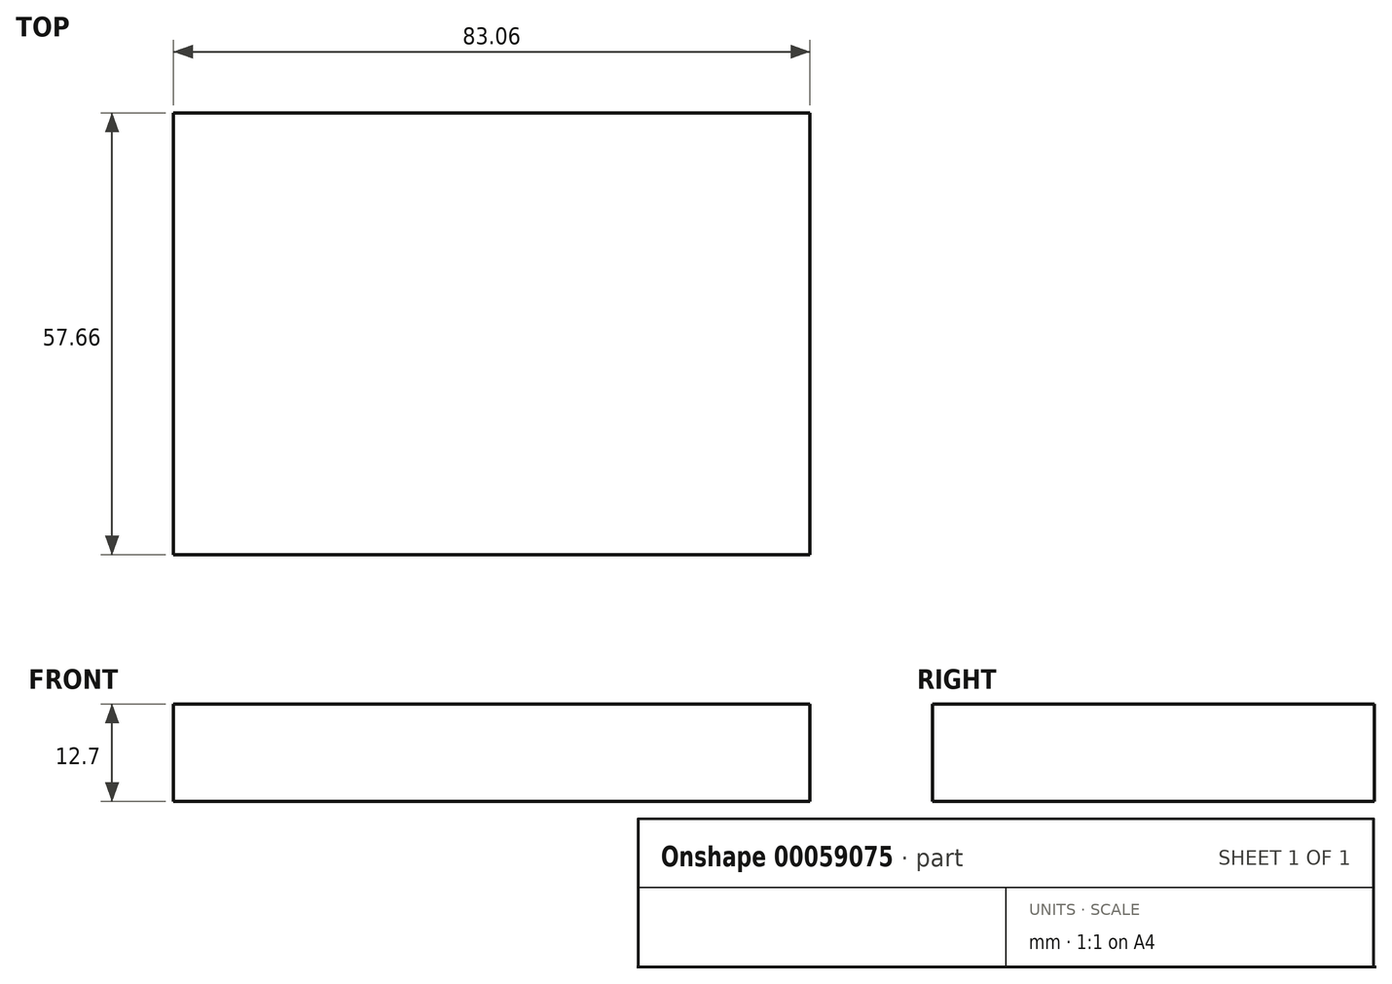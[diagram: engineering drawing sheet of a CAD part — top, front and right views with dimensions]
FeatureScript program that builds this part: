
annotation { "Feature Type Name" : "Feature", "Feature Type Description" : "" }
export const myFeature = defineFeature(function(context is Context, id is Id, definition is map)
    precondition{}
    {
        {
            var Q0;
            Q0=qCreatedBy(makeId("Top.planeOp"),FACE);
            var sketch = newSketch(context, id + "F0", { "sketchPlane" : qUnion([Q0])});
            skLineSegment(sketch, "E0.bottom", {"start": v(48.12, -28.78) * mm, "end": v(-34.94, -28.78) * mm});
            skLineSegment(sketch, "E0.top", {"start": v(48.12, 28.88) * mm, "end": v(-34.94, 28.88) * mm});
            skLineSegment(sketch, "E0.left", {"start": v(48.12, -28.78) * mm, "end": v(48.12, 28.88) * mm});
            skLineSegment(sketch, "E0.right", {"start": v(-34.94, -28.78) * mm, "end": v(-34.94, 28.88) * mm});
            skSolve(sketch);
        }
        {
            var Q0;
            Q0=makeQuery(id+"F0.imprint","IMPRINT",FACE,{"disambiguationData":[TD([[makeQuery(id+"F0.imprint","IMPRINT",EDGE,{"derivedFrom":sQuery(id+"F0.wireOp",EDGE,"E0.bottom")}),-1.0]])]});
            extrude(context, id + "F1", {"entities" : qUnion([Q0]), "oppositeDirection" : true, "depth" : 12.7 * mm});
        }
    });
